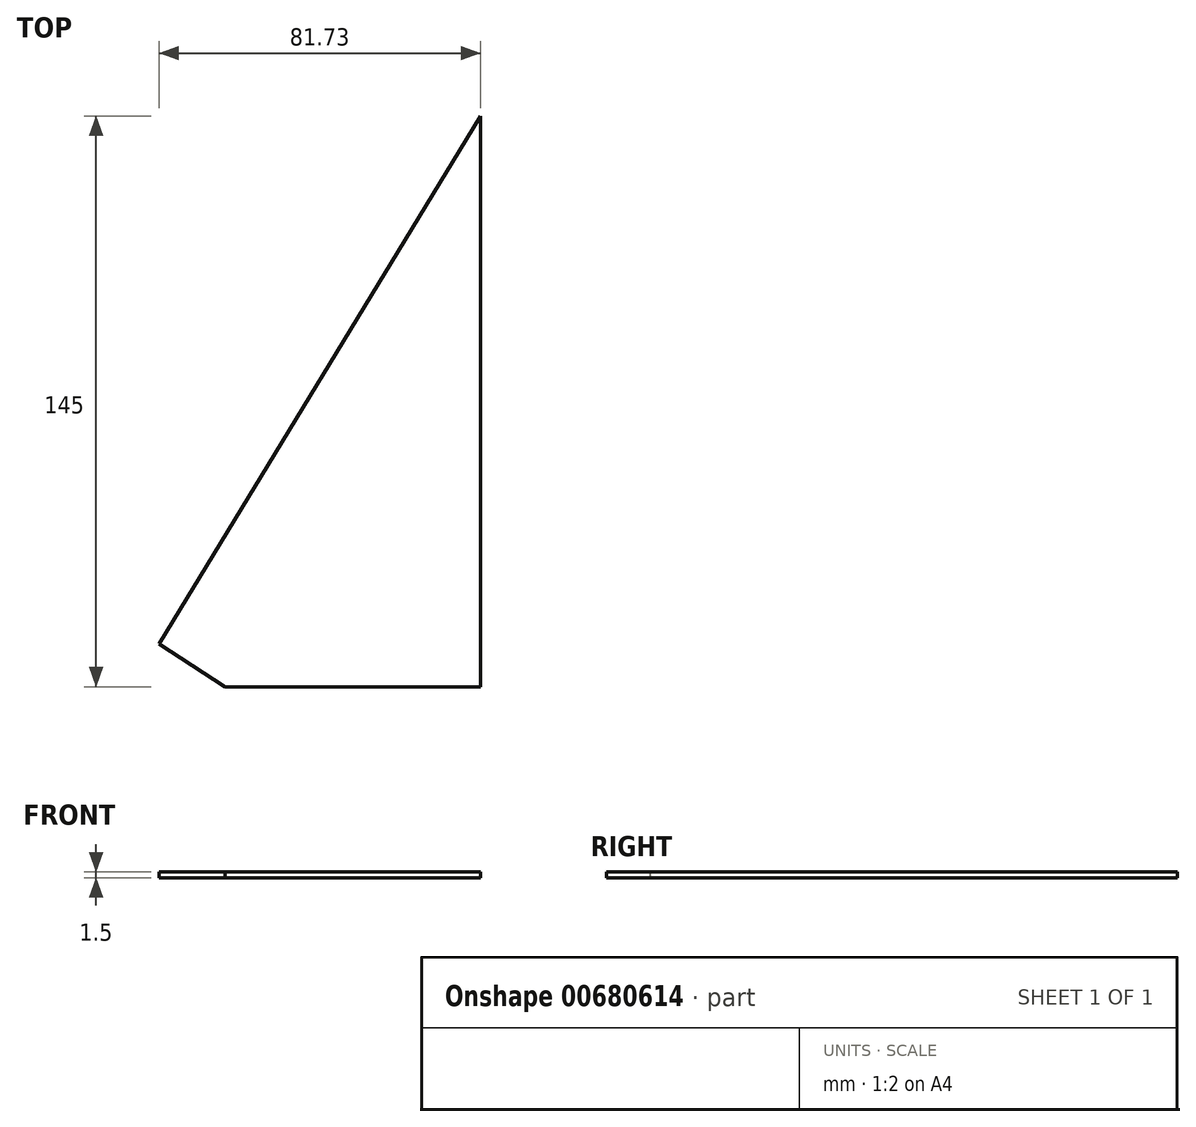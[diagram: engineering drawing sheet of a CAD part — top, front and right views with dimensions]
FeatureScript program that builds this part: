
annotation { "Feature Type Name" : "Feature", "Feature Type Description" : "" }
export const myFeature = defineFeature(function(context is Context, id is Id, definition is map)
    precondition{}
    {
        {
            var Q0;
            Q0=qCreatedBy(makeId("Top.planeOp"),FACE);
            var sketch = newSketch(context, id + "F0", { "sketchPlane" : qUnion([Q0])});
            skLineSegment(sketch, "E0", {"start": v(0, 0) * mm, "end": v(0, 145) * mm});
            skLineSegment(sketch, "E1", {"start": v(0, 145) * mm, "end": v(-81.73, 10.95) * mm});
            skLineSegment(sketch, "E2", {"start": v(-81.73, 10.95) * mm, "end": v(-65, 0) * mm});
            skLineSegment(sketch, "E3", {"start": v(-65, 0) * mm, "end": v(0, 0) * mm});
            skSolve(sketch);
        }
        {
            var Q0;
            Q0=makeQuery(id+"F0.imprint","IMPRINT",FACE,{"disambiguationData":[TD([[makeQuery(id+"F0.imprint","IMPRINT",EDGE,{"derivedFrom":sQuery(id+"F0.wireOp",EDGE,"E0")}),1.0]])]});
            extrude(context, id + "F1", {"entities" : qUnion([Q0]), "depth" : 1.5 * mm, "offsetDistance" : 25 * mm});
        }
    });
